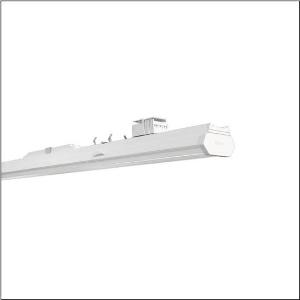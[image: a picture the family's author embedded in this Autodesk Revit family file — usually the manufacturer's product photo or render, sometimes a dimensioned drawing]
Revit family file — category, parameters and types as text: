
# Revit family: licross_11_protected_mo_51td127n485g
name_source: partatom
category: Lighting Fixtures
units: mm (PartAtom-declared; Revit-internal decimal feet)

## family parameters
Cut with Voids When Loaded = No
Host = Face
Light Source = No
Part Type = Normal
Room Calculation Point = No
Round Connector Dimension = Use Diameter
Shared = No

## types (1)
- Licross 11 Protected MO (1 x LED, 8720 lm, 48.6 W, 4000K)
    Apparent Load = 49 VA
    CIE Flux Codes = 73 92 98 99 100
    Color Rendering = 80
    Color Temperature = 4000K
    Default Elevation = 1800 mm
    Description = Licross 11 Protected MO, luminaire insert, of sheet steel, galvanised, coil coated, white, length: 1.500mm, width: 90mm, height: 101mm, LED rated luminous flux: 8.720lm, light colour: 840, SDCM (Standard Deviation of Colour Matching)MacAdam ≤ 2 SDCM (initial), control gear: ON/OFF, with plug, 3-pole, with phase selection, mains connection: 220..240V, AC, 50/60Hz, rated input power: 49W, internal wiring halogen-free, primary light control with lens, of plastic, primary optical cover: cover, of PMMA, light emission: direct distribution, primary light characteristic: symmetric, protection rating (complete): IP54, insulation class (complete): insulation class I (protective earthing), certification: CE, ENEC, VDE, UKCA, protection symbol: D if used in an environment with non-conductive dust loads with corresponding accessories, impact resistance: IK06, permissible ambient temperature for indoor applications: -25..+35°C, corresponds to IFS (International Featured Standards) requirements for safety and quality in the food industry, reducing of maximum allowable ambient temperature of 5°C with ceiling mounting, LABS conformity tested according to VDMA 24364:2018-05, The light source and the operating device comply with the requirements of the Ecodesign Regulation (EU) 2019/2020 and are replaceable in accordance with this regulation, packaging unit: 1 piece
    Height = 92 mm
    Lamp = 1 x LED
    Lamp Light Flux = 8720 lm
    Lamp Power = 48.6 W
    Lamp count = 1
    Length = 1500 mm
    Luminous efficacy = 179 lm/W
    Manufacturer = Siteco
    ModVariant = No
    Model = 51TD127N485G
    Mounting Place = Ceiling
    Mounting Type = Pendant
    Number of Poles = 1
    OnlyDefault = Yes
    Power Factor = 1
    Product Name = Licross 11 Protected MO
    Product group = luminaire insert | ceiling pendant
    ProductGroupID = 901
    Protection Class = Protection class I
    Protection Degree = IP 54
    RLX_Detail_Level = 1
    RLX_Emergency_Light_Flux = 0 lm
    RLX_Emergency_Type = 0
    RLX_Emergency_Type_DB = No
    RlxData = <blob elided: 20949 chars, md5=6219c05d>
    Socket = socket
    Standby Power = 0 W
    System Light Flux = 8720 lm
    System Power = 49 W
    Type Comments = Product without accessories
    Type Image = l_1256145.jpg
    URL = http://relux.com
    VarID = ---
    Voltage = 0 V
    Weight = 0.00 kg
    Width = 88 mm

## geometry (parser evidence)
native form markers: Blend x4, Sweep x10
no freeform markers — native parametric forms only
